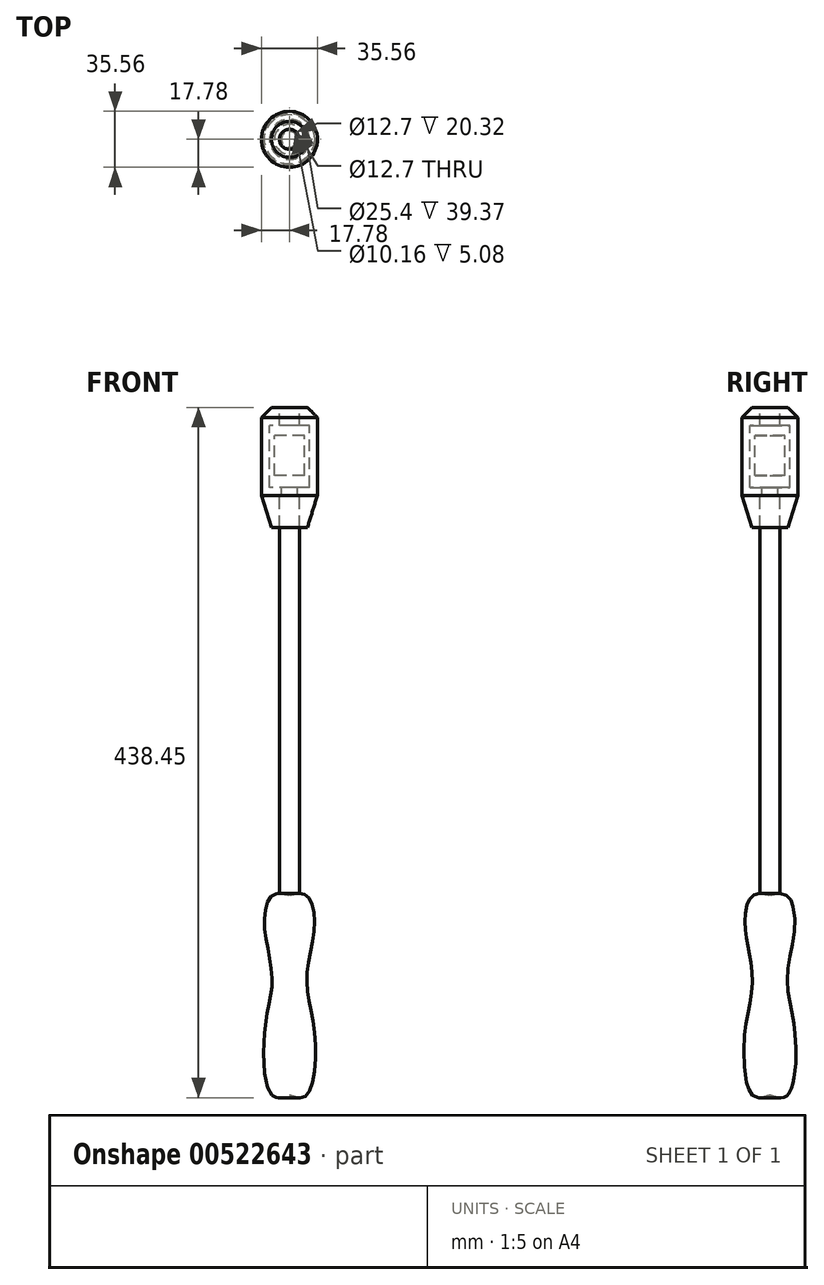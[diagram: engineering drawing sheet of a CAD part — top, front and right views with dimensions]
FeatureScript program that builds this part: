
annotation { "Feature Type Name" : "Feature", "Feature Type Description" : "" }
export const myFeature = defineFeature(function(context is Context, id is Id, definition is map)
    precondition{}
    {
        {
            var Q0;
            Q0=qCreatedBy(makeId("Front.planeOp"),FACE);
            var sketch = newSketch(context, id + "F0", { "sketchPlane" : qUnion([Q0])});
            skLineSegment(sketch, "E0", {"start": v(0, 292.1) * mm, "end": v(0, 266.7) * mm});
            skLineSegment(sketch, "E1", {"start": v(0, 266.7) * mm, "end": v(9.52, 266.7) * mm});
            skLineSegment(sketch, "E2", {"start": v(9.53, 266.7) * mm, "end": v(9.53, 292.1) * mm});
            skLineSegment(sketch, "E3", {"start": v(9.52, 292.1) * mm, "end": v(0, 292.1) * mm});
            skLineSegment(sketch, "E4", {"start": v(0, 266.7) * mm, "end": v(0, 0) * mm, "construction": true});
            skLineSegment(sketch, "E5.bottom", {"start": v(0, 0) * mm, "end": v(15.88, 0) * mm, "construction": true});
            skLineSegment(sketch, "E5.top", {"start": v(0, -127) * mm, "end": v(15.88, -127) * mm, "construction": true});
            skLineSegment(sketch, "E5.left", {"start": v(0, 0) * mm, "end": v(0, -127) * mm});
            skLineSegment(sketch, "E5.right", {"start": v(15.88, 0) * mm, "end": v(15.88, -127) * mm, "construction": true});
            skLineSegment(sketch, "E6.bottom", {"start": v(0, 254) * mm, "end": v(6.35, 254) * mm});
            skLineSegment(sketch, "E6.top", {"start": v(0, -127) * mm, "end": v(6.35, -127) * mm});
            skLineSegment(sketch, "E6.left", {"start": v(0, 254) * mm, "end": v(0, -127) * mm});
            skLineSegment(sketch, "E6.right", {"start": v(6.35, 254) * mm, "end": v(6.35, -127) * mm});
            skLineSegment(sketch, "E7", {"start": v(6.35, 233.68) * mm, "end": v(11.43, 233.68) * mm});
            skLineSegment(sketch, "E8", {"start": v(11.43, 233.68) * mm, "end": v(17.78, 254) * mm});
            skLineSegment(sketch, "E9", {"start": v(17.78, 254) * mm, "end": v(17.78, 303.53) * mm});
            skLineSegment(sketch, "E10", {"start": v(17.78, 303.53) * mm, "end": v(11.43, 309.88) * mm});
            skLineSegment(sketch, "E11", {"start": v(11.43, 309.88) * mm, "end": v(6.35, 309.88) * mm});
            skLineSegment(sketch, "E12", {"start": v(6.35, 309.88) * mm, "end": v(6.35, 298.45) * mm});
            skLineSegment(sketch, "E13", {"start": v(6.35, 298.45) * mm, "end": v(12.7, 298.45) * mm});
            skLineSegment(sketch, "E14", {"start": v(12.7, 298.45) * mm, "end": v(12.7, 259.08) * mm});
            skLineSegment(sketch, "E15", {"start": v(12.7, 259.08) * mm, "end": v(5.08, 259.08) * mm});
            skLineSegment(sketch, "E16", {"start": v(5.08, 259.08) * mm, "end": v(5.08, 254) * mm});
            skLineSegment(sketch, "E17", {"start": v(12.7, 298.45) * mm, "end": v(17.78, 303.53) * mm, "construction": true});
            skLineSegment(sketch, "E18", {"start": v(12.7, 259.08) * mm, "end": v(17.78, 254) * mm, "construction": true});
            skFitSpline(sketch, "E19", {"points": [v(0, 0) * mm, v(10.56, 0) * mm, v(15.88, -18.28) * mm, v(11.03, -52.84) * mm, v(15.88, -86.7) * mm, v(11.03, -127) * mm, v(0, -127) * mm], "startDerivative": vector(104.05, 24.98) * mm, "endDerivative": vector(-107.26, 35.58) * mm});
            skSolve(sketch);
        }
        {
            var Q0;
            Q0=makeQuery(id+"F0.imprint","IMPRINT",FACE,{"disambiguationData":[TD([[makeQuery(id+"F0.imprint","IMPRINT",EDGE,{"derivedFrom":sQuery(id+"F0.wireOp",EDGE,"E0")}),1.0]])]});
            var Q1;
            Q1=sQuery(id+"F0.wireOp",EDGE,"E4");
            revolve(context, id + "F1", {"entities" : qUnion([Q0]), "axis" : qUnion([Q1]), "revolveType" : RevolveType.FULL});
        }
        {
            var Q0;
            {var subQ5=sQuery(id+"F0.wireOp",EDGE,"E6.bottom");Q0=makeQuery(id+"F0.imprint","IMPRINT",FACE,{"disambiguationData":[TD([[makeQuery(id+"F0.imprint","IMPRINT",EDGE,{"derivedFrom":subQ5}),-1.0]])]});}
            var Q1;
            Q1=sQuery(id+"F0.wireOp",EDGE,"E4");
            revolve(context, id + "F2", {"entities" : qUnion([Q0]), "axis" : qUnion([Q1]), "revolveType" : RevolveType.FULL});
        }
        {
            var Q0;
            {var subQ0=sQuery(id+"F0.wireOp",EDGE,"E6.top");Q0=makeQuery(id+"F0.imprint","IMPRINT",FACE,{"disambiguationData":[TD([[makeQuery(id+"F0.imprint","IMPRINT",EDGE,{"derivedFrom":subQ0}),-1.0]])]});}
            var Q1;
            {var subQ0=sQuery(id+"F0.wireOp",EDGE,"E6.top");Q1=makeQuery(id+"F0.imprint","IMPRINT",FACE,{"disambiguationData":[TD([[makeQuery(id+"F0.imprint","IMPRINT",EDGE,{"derivedFrom":subQ0}),1.0]])]});}
            var Q2;
            Q2=sQuery(id+"F0.wireOp",EDGE,"E4");
            revolve(context, id + "F3", {"entities" : qUnion([Q0, Q1]), "axis" : qUnion([Q2]), "revolveType" : RevolveType.FULL});
        }
        {
            var Q0;
            {var subQ4=sQuery(id+"F0.wireOp",EDGE,"E7");Q0=makeQuery(id+"F0.imprint","IMPRINT",FACE,{"disambiguationData":[TD([[makeQuery(id+"F0.imprint","IMPRINT",EDGE,{"derivedFrom":subQ4}),1.0]])]});}
            var Q1;
            Q1=sQuery(id+"F0.wireOp",EDGE,"E4");
            revolve(context, id + "F4", {"entities" : qUnion([Q0]), "axis" : qUnion([Q1]), "revolveType" : RevolveType.FULL});
        }
    });
